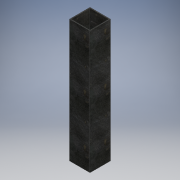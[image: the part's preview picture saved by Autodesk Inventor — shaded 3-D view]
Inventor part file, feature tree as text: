
AUTODESK INVENTOR PART (.ipt)
format: ipt  version: 2017 (Build 210142000, 142)  size: 112,128 bytes
history: native  units: mm
features: other x1, extrude x1, sketch x1
ambient origin geometry x8: Origin, YZ Plane, XZ Plane, XY Plane, X Axis, Y Axis, Z Axis, Center Point
bodies: Body1 (feature_tree)
feature tree (3):
  other  "Sólido1"
  extrude  "Extrusión1"  Depth=75.0mm
  sketch  "Boceto1"  dims[d0=75.0mm d1=75.0mm d2=3.0mm d3=37.5mm d4=37.5mm d5=450.0mm d6=0.0mm]
